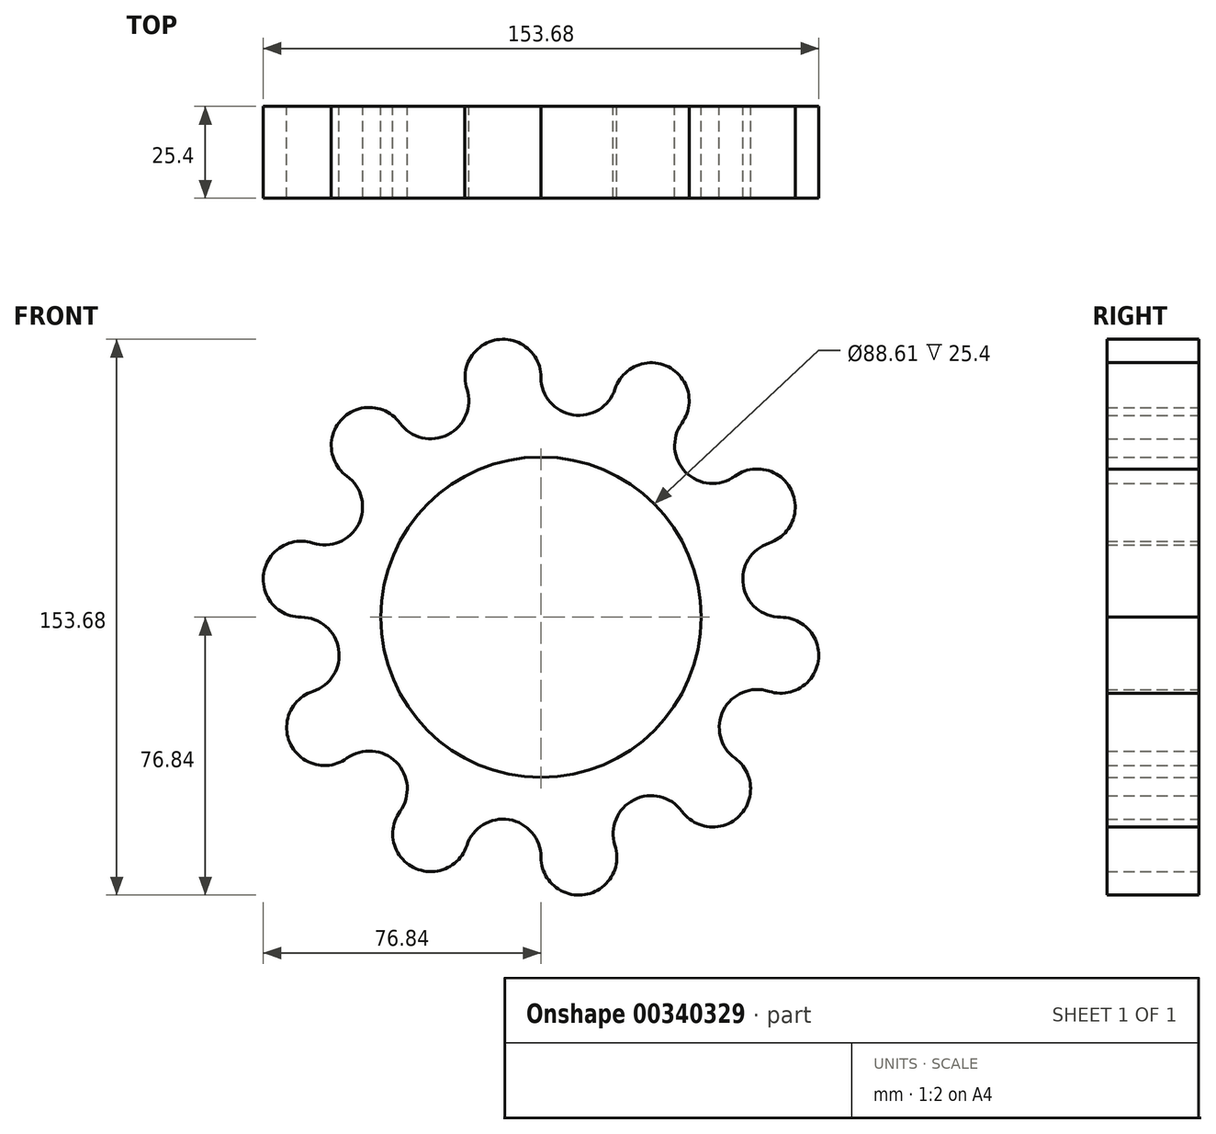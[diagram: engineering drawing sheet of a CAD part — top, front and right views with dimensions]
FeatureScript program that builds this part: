
annotation { "Feature Type Name" : "Feature", "Feature Type Description" : "" }
export const myFeature = defineFeature(function(context is Context, id is Id, definition is map)
    precondition{}
    {
        {
            var Q0;
            Q0=qCreatedBy(makeId("Front.planeOp"),FACE);
            var sketch = newSketch(context, id + "F0", { "sketchPlane" : qUnion([Q0])});
            skArc(sketch, "E0", {"start": v(-20.5, 63.09) * mm, "mid": v(-12.15, 76.71) * mm, "end": v(0, 66.33) * mm});
            skArc(sketch, "E1.1.0", {"start": v(-53.67, 38.99) * mm, "mid": v(-54.92, 54.92) * mm, "end": v(-38.99, 53.67) * mm});
            skArc(sketch, "E1.2.0", {"start": v(-66.33, 0) * mm, "mid": v(-76.71, 12.15) * mm, "end": v(-63.09, 20.5) * mm});
            skArc(sketch, "E1.3.0", {"start": v(-53.67, -38.99) * mm, "mid": v(-69.2, -35.26) * mm, "end": v(-63.09, -20.5) * mm});
            skArc(sketch, "E1.4.0", {"start": v(-20.5, -63.09) * mm, "mid": v(-35.26, -69.2) * mm, "end": v(-38.99, -53.67) * mm});
            skArc(sketch, "E1.5.0", {"start": v(20.5, -63.09) * mm, "mid": v(12.15, -76.71) * mm, "end": v(0, -66.33) * mm});
            skArc(sketch, "E1.6.0", {"start": v(53.67, -38.99) * mm, "mid": v(54.92, -54.92) * mm, "end": v(38.99, -53.67) * mm});
            skArc(sketch, "E1.7.0", {"start": v(66.33, 0) * mm, "mid": v(76.71, -12.15) * mm, "end": v(63.09, -20.5) * mm});
            skArc(sketch, "E1.8.0", {"start": v(53.67, 38.99) * mm, "mid": v(69.2, 35.26) * mm, "end": v(63.09, 20.5) * mm});
            skArc(sketch, "E1.9.0", {"start": v(20.5, 63.09) * mm, "mid": v(35.26, 69.2) * mm, "end": v(38.99, 53.67) * mm});
            skPoint(sketch, "E1.center", {"position": v(0, 0) * mm});
            skCircle(sketch, "E2", {"center": v(0, 0) * mm, "radius": 21.14 * mm});
            skPoint(sketch, "E3.endSnap0", {"position": v(35.26, 69.2) * mm});
            skArc(sketch, "E4", {"start": v(-38.99, 53.67) * mm, "mid": v(-25.72, 50.48) * mm, "end": v(-20.5, 63.09) * mm});
            skArc(sketch, "E5.1.0", {"start": v(-63.09, 20.5) * mm, "mid": v(-50.48, 25.72) * mm, "end": v(-53.67, 38.99) * mm});
            skArc(sketch, "E5.2.0", {"start": v(-63.09, -20.5) * mm, "mid": v(-55.96, -8.86) * mm, "end": v(-66.33, 0) * mm});
            skArc(sketch, "E5.3.0", {"start": v(-38.99, -53.67) * mm, "mid": v(-40.06, -40.06) * mm, "end": v(-53.67, -38.99) * mm});
            skArc(sketch, "E5.4.0", {"start": v(0, -66.33) * mm, "mid": v(-8.86, -55.96) * mm, "end": v(-20.5, -63.09) * mm});
            skArc(sketch, "E5.5.0", {"start": v(38.99, -53.67) * mm, "mid": v(25.72, -50.48) * mm, "end": v(20.5, -63.09) * mm});
            skArc(sketch, "E5.6.0", {"start": v(63.09, -20.5) * mm, "mid": v(50.48, -25.72) * mm, "end": v(53.67, -38.99) * mm});
            skArc(sketch, "E5.7.0", {"start": v(63.09, 20.5) * mm, "mid": v(55.96, 8.86) * mm, "end": v(66.33, 0) * mm});
            skArc(sketch, "E5.8.0", {"start": v(38.99, 53.67) * mm, "mid": v(40.06, 40.06) * mm, "end": v(53.67, 38.99) * mm});
            skArc(sketch, "E5.9.0", {"start": v(0, 66.33) * mm, "mid": v(8.86, 55.96) * mm, "end": v(20.5, 63.09) * mm});
            skCircle(sketch, "E6", {"center": v(0, 0) * mm, "radius": 44.3 * mm});
            skFitSpline(sketch, "E7", {"points": [v(-5.63, 43.94) * mm, v(0, 38.07) * mm], "startDerivative": vector(0, 0) * mm, "endDerivative": vector(0, -9.37) * mm});
            skFitSpline(sketch, "E8", {"points": [v(-6.64, 20.07) * mm, v(0, 28.75) * mm], "startDerivative": vector(8.9, 2.24) * mm, "endDerivative": vector(0, 10.37) * mm});
            skFitSpline(sketch, "E9.MirrorCS", {"points": [v(18.52, 40.25) * mm, v(9.85, 36.75) * mm], "startDerivative": vector(-10.31, 4.23) * mm, "endDerivative": vector(-2.42, -9.04) * mm});
            skFitSpline(sketch, "E10.MirrorCS", {"points": [v(11.61, 17.67) * mm, v(7.44, 27.77) * mm], "startDerivative": vector(-8, 4.47) * mm, "endDerivative": vector(2.68, 10.02) * mm});
            skLineSegment(sketch, "E11", {"start": v(0, 28.75) * mm, "end": v(0, 38.07) * mm});
            skLineSegment(sketch, "E12", {"start": v(9.85, 36.75) * mm, "end": v(7.44, 27.77) * mm});
            skLineSegment(sketch, "E13.1.0", {"start": v(-31.91, 20.72) * mm, "end": v(-24.1, 15.66) * mm});
            skLineSegment(sketch, "E13.1.1", {"start": v(-27.34, 8.88) * mm, "end": v(-36.2, 11.76) * mm});
            skLineSegment(sketch, "E13.2.0", {"start": v(-29.57, -23.95) * mm, "end": v(-22.34, -18.1) * mm});
            skLineSegment(sketch, "E13.2.1", {"start": v(-16.9, -23.26) * mm, "end": v(-22.37, -30.8) * mm});
            skLineSegment(sketch, "E13.3.0", {"start": v(13.64, -35.52) * mm, "end": v(10.3, -26.84) * mm});
            skLineSegment(sketch, "E13.3.1", {"start": v(16.9, -23.26) * mm, "end": v(22.38, -30.8) * mm});
            skLineSegment(sketch, "E13.4.0", {"start": v(38, 2) * mm, "end": v(28.7, 1.5) * mm});
            skLineSegment(sketch, "E13.4.1", {"start": v(27.34, 8.88) * mm, "end": v(36.2, 11.77) * mm});
            skSolve(sketch);
        }
        {
            var Q0;
            Q0 = qSketchRegion(id + "F0", true);
            extrude(context, id + "F1", {"entities" : qUnion([Q0]), "endBound" : BoundingType.SYMMETRIC, "depth" : 25.4 * mm});
        }
    });
